# Revit family: Haworth_Intuity_Benching_DoubleSided
name_source: partatom
category: Furniture Systems
revit_build: Autodesk Revit 2018 (Build: 20170223_1515(x64)
units: mm (PartAtom-declared; Revit-internal decimal feet)

## family parameters
Always vertical = Yes
Cut with Voids When Loaded = No
OmniClass Number = 23.40.70.14.64.21
OmniClass Title = Systems Furniture
Part Type = Normal
Room Calculation Point = No
Round Connector Dimension = Use Diameter
Shared = No
Work Plane-Based = No

## types (10) — shared parameters
Access Hatch No = No
Access Hatch Yes = Yes
Access Plate Depth = 4 1/4"
Access Plate Height = 3/8"
Access Plate Offset = 7/8"
Actual Height = 29 3/16"
Assembly Code = E2020200
Beam Depth = 1 1/4"
Beam Gap = 9/16"
Beam Height = 2"
Beam Offset = 16 1/2"
Custom Screen Size = No
Custom Size = No
Description = Haworth - Intuity - Benching - Double Sided
End Cap Depth Half = 5 29/32"
End Cap Offset = 1/8"
Leg Half = 1"
Leg Height = 28"
Manufacturer = Haworth
Max Screen Width = 60"
Max Width = 72"
Min Screen Width = 24"
Min Width = 48"
Model = Haworth - Intuity - Benching - Double Sided
Revision Number = 2
Screen Height - 13 in. = Yes
Screen Height - 21 in. = No
Size = Verify Final Dim. w/ Haworth
Standard Bench Widths = 48, 54, 60, 66, 72 inches
Standard Screen Widths = 24, 30, 36, 42, 48, 54, 60 inches
Sustainability Info = https://www.haworth.com
Top Thickness = 1 3/16"
URL = https://www.haworth.com
URL - Product = http://www.haworth.com
Utility Tray Yes = Yes
Warranty = http://www.haworth.com
Worksurface Finish = Haworth _ Laminate _ Linen H-WL

## per-type parameters (varying)
| type | 48 Depth | 60 Depth | Accent Plate Finish | Access Hatch Finish | Actual Depth | Actual Screen Width | Actual Width | Actual Worksurface Depth | Leg Finish | Rail Finish | Screen Finish | Screen Width | Width | Worksurface Depth |
| 24d 48w | Yes | No | Haworth _ Paint _ Metallic Silver | Haworth _ Paint _ Metallic Silver | 50 13/16" | 47 3/4" | 48" | 19 1/2" | Haworth _ Paint _ Metallic Silver | Haworth _ Paint _ Metallic Silver | Haworth _ Fabric _ Tellure _ Geranium 3A-42 | 48" | 48" | 24" |
| 24d 54w | Yes | No | Haworth _ Paint _ Metallic Silver | Haworth _ Paint _ Metallic Silver | 50 13/16" | 53 3/4" | 54" | 19 1/2" | Haworth _ Paint _ Metallic Silver | Haworth _ Paint _ Metallic Silver | Haworth _ Fabric _ Tellure _ Geranium 3A-42 | 54" | 54" | 24" |
| 24d 60w | Yes | No | Haworth _ Paint _ Metallic Silver | Haworth _ Paint _ Metallic Silver | 50 13/16" | 59 3/4" | 60" | 19 1/2" | Haworth _ Paint _ Metallic Silver | Haworth _ Paint _ Metallic Silver | Haworth _ Fabric _ Tellure _ Geranium 3A-42 | 60" | 60" | 24" |
| 24d 66w | Yes | No | Haworth _ Paint _ Metallic Silver | Haworth _ Paint _ Metallic Silver | 50 13/16" | 59 3/4" | 66" | 19 1/2" | Haworth _ Paint _ Metallic Silver | Haworth _ Paint _ Metallic Silver | Haworth _ Fabric _ Tellure _ Geranium 3A-42 | 60" | 66" | 24" |
| 24d 72w | Yes | No | Haworth _ Paint _ Metallic Silver | Haworth _ Paint _ Metallic Silver | 50 13/16" | 59 3/4" | 72" | 19 1/2" | Haworth _ Paint _ Metallic Silver | Haworth _ Paint _ Metallic Silver | Haworth _ Fabric _ Tellure _ Geranium 3A-42 | 60" | 72" | 24" |
| 30d 48w | No | Yes | Haworth _ Paint _ Polar | Haworth _ Paint _ Polar | 62 13/16" | 47 3/4" | 48" | 25 1/2" | Haworth _ Paint _ Polar | Haworth _ Paint _ Polar | Haworth _ Fabric _ Tellure _ Ocean 3A-34 | 48" | 48" | 30" |
| 30d 54w | No | Yes | Haworth _ Paint _ Metallic Silver | Haworth _ Paint _ Metallic Silver | 62 13/16" | 53 3/4" | 54" | 25 1/2" | Haworth _ Paint _ Metallic Silver | Haworth _ Paint _ Metallic Silver | Haworth _ Fabric _ Tellure _ Geranium 3A-42 | 54" | 54" | 30" |
| 30d 60w | No | Yes | Haworth _ Paint _ Metallic Silver | Haworth _ Paint _ Metallic Silver | 62 13/16" | 59 3/4" | 60" | 25 1/2" | Haworth _ Paint _ Metallic Silver | Haworth _ Paint _ Metallic Silver | Haworth _ Fabric _ Tellure _ Geranium 3A-42 | 60" | 60" | 30" |
| 30d 66w | No | Yes | Haworth _ Paint _ Metallic Silver | Haworth _ Paint _ Metallic Silver | 62 13/16" | 59 3/4" | 66" | 25 1/2" | Haworth _ Paint _ Metallic Silver | Haworth _ Paint _ Metallic Silver | Haworth _ Fabric _ Tellure _ Geranium 3A-42 | 60" | 66" | 30" |
| 30d 72w | No | Yes | Haworth _ Paint _ Metallic Silver | Haworth _ Paint _ Metallic Silver | 62 13/16" | 59 3/4" | 72" | 25 1/2" | Haworth _ Paint _ Metallic Silver | Haworth _ Paint _ Metallic Silver | Haworth _ Fabric _ Tellure _ Geranium 3A-42 | 60" | 72" | 30" |

## geometry (parser evidence)
native form markers: Sweep x22
no freeform markers — native parametric forms only
